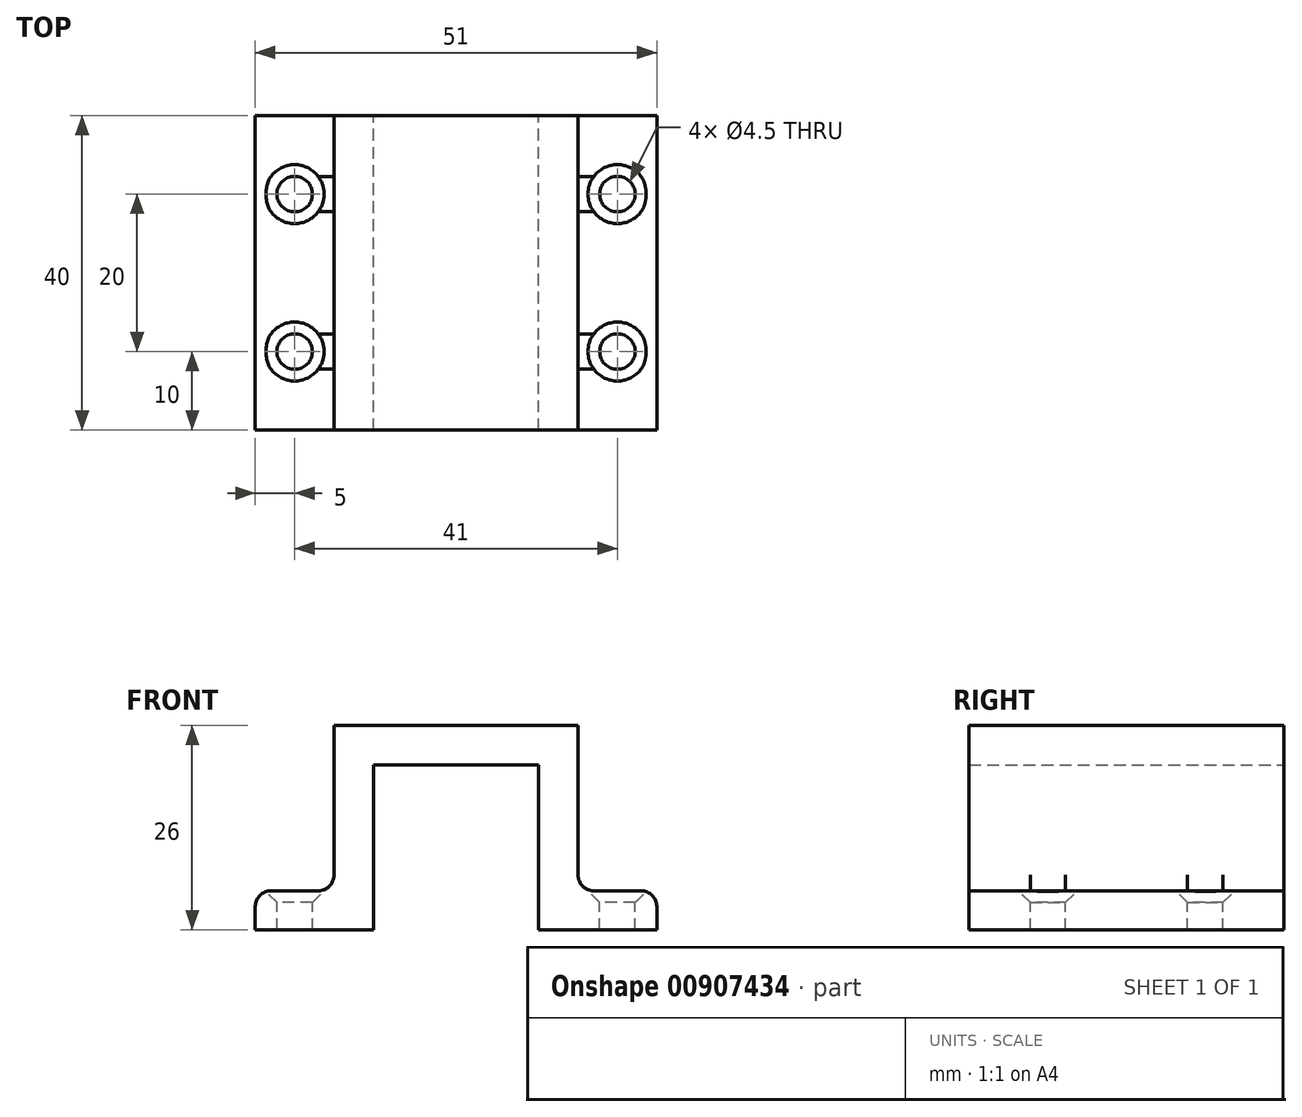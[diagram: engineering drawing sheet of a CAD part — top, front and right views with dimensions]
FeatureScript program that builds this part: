
annotation { "Feature Type Name" : "Feature", "Feature Type Description" : "" }
export const myFeature = defineFeature(function(context is Context, id is Id, definition is map)
    precondition{}
    {
        {
            var Q0;
            Q0=qCreatedBy(makeId("Front.planeOp"),FACE);
            var sketch = newSketch(context, id + "F0", { "sketchPlane" : qUnion([Q0])});
            skLineSegment(sketch, "E0", {"start": v(10.5, 0) * mm, "end": v(21, 0) * mm});
            skLineSegment(sketch, "E1", {"start": v(21, 0) * mm, "end": v(21, -21) * mm});
            skLineSegment(sketch, "E2", {"start": v(21, -21) * mm, "end": v(31, -21) * mm});
            skLineSegment(sketch, "E3", {"start": v(31, -16) * mm, "end": v(26, -16) * mm});
            skLineSegment(sketch, "E4", {"start": v(26, -16) * mm, "end": v(26, 5) * mm});
            skLineSegment(sketch, "E5.0", {"start": v(10.5, 5) * mm, "end": v(21, 5) * mm});
            skLineSegment(sketch, "E6", {"start": v(21, 5) * mm, "end": v(26, 5) * mm});
            skPoint(sketch, "E7.orphan", {"position": v(0, 0) * mm});
            skLineSegment(sketch, "E8.MirrorCS", {"start": v(10.5, 5) * mm, "end": v(0, 5) * mm});
            skLineSegment(sketch, "E9.MirrorCS", {"start": v(0, 5) * mm, "end": v(-5, 5) * mm});
            skLineSegment(sketch, "E10.MirrorCS", {"start": v(10.5, 0) * mm, "end": v(0, 0) * mm});
            skLineSegment(sketch, "E11.MirrorCS", {"start": v(-5, -16) * mm, "end": v(-5, 5) * mm});
            skLineSegment(sketch, "E12.MirrorCS", {"start": v(0, 0) * mm, "end": v(0, -21) * mm});
            skLineSegment(sketch, "E13.MirrorCS", {"start": v(0, -21) * mm, "end": v(-10, -21) * mm});
            skLineSegment(sketch, "E14.MirrorCS", {"start": v(-10, -16) * mm, "end": v(-5, -16) * mm});
            skLineSegment(sketch, "E15", {"start": v(31, -16) * mm, "end": v(36, -16) * mm});
            skLineSegment(sketch, "E16", {"start": v(36, -16) * mm, "end": v(36, -21) * mm});
            skLineSegment(sketch, "E17", {"start": v(36, -21) * mm, "end": v(31, -21) * mm});
            skLineSegment(sketch, "E18.MirrorCS", {"start": v(-10, -16) * mm, "end": v(-15, -16) * mm});
            skLineSegment(sketch, "E19.MirrorCS", {"start": v(-15, -16) * mm, "end": v(-15, -21) * mm});
            skLineSegment(sketch, "E20.MirrorCS", {"start": v(-15, -21) * mm, "end": v(-10, -21) * mm});
            skSolve(sketch);
        }
        {
            var Q0;
            Q0 = qSketchRegion(id + "F0", true);
            extrude(context, id + "F1", {"entities" : qUnion([Q0]), "depth" : 40 * mm, "offsetDistance" : 25 * mm});
        }
        {
            var Q0;
            Q0=makeQuery(id+"F1.opExtrude","SWEPT_FACE",FACE,{"disambiguationData":[OSD([sQuery(id+"F0.wireOp",EDGE,"E5.0"),sQuery(id+"F0.wireOp",EDGE,"E6"),sQuery(id+"F0.wireOp",EDGE,"E8.MirrorCS"),sQuery(id+"F0.wireOp",EDGE,"E9.MirrorCS")])]});
            var sketch = newSketch(context, id + "F2", { "sketchPlane" : qUnion([Q0])});
            skLineSegment(sketch, "E21", {"start": v(26, 0) * mm, "end": v(36, 0) * mm});
            skCircle(sketch, "E22", {"center": v(31, -10) * mm, "radius": 2.25 * mm});
            skCircle(sketch, "E23.MirrorC", {"center": v(31, -30) * mm, "radius": 2.25 * mm});
            skCircle(sketch, "E24.MirrorC", {"center": v(-10, -10) * mm, "radius": 2.25 * mm});
            skCircle(sketch, "E25.MirrorC", {"center": v(-10, -30) * mm, "radius": 2.25 * mm});
            skSolve(sketch);
        }
        {
            var Q0;
            Q0 = qSketchRegion(id + "F2", true);
            extrude(context, id + "F3", {"entities" : qUnion([Q0]), "operationType" : NewBodyOperationType.REMOVE, "endBound" : BoundingType.THROUGH_ALL, "oppositeDirection" : true, "depth" : 25 * mm, "offsetDistance" : 25 * mm});
        }
        {
            var Q0;
            Q0=makeQuery(id+"F3.boolean.opBoolean","INTERSECT",EDGE,{"derivedFrom":[makeQuery(id+"F1.opExtrude","SWEPT_FACE",FACE,{"disambiguationData":[OSD([sQuery(id+"F0.wireOp",EDGE,"E14.MirrorCS"),sQuery(id+"F0.wireOp",EDGE,"E18.MirrorCS")])]}),makeQuery(id+"F3.opExtrude","SWEPT_FACE",FACE,{"disambiguationData":[OSD([sQuery(id+"F2.wireOp",EDGE,"E24.MirrorC")])]})]});
            var Q1;
            Q1=makeQuery(id+"F3.boolean.opBoolean","INTERSECT",EDGE,{"derivedFrom":[makeQuery(id+"F1.opExtrude","SWEPT_FACE",FACE,{"disambiguationData":[OSD([sQuery(id+"F0.wireOp",EDGE,"E14.MirrorCS"),sQuery(id+"F0.wireOp",EDGE,"E18.MirrorCS")])]}),makeQuery(id+"F3.opExtrude","SWEPT_FACE",FACE,{"disambiguationData":[OSD([sQuery(id+"F2.wireOp",EDGE,"E25.MirrorC")])]})]});
            var Q2;
            Q2=makeQuery(id+"F3.boolean.opBoolean","INTERSECT",EDGE,{"derivedFrom":[makeQuery(id+"F1.opExtrude","SWEPT_FACE",FACE,{"disambiguationData":[OSD([sQuery(id+"F0.wireOp",EDGE,"E3"),sQuery(id+"F0.wireOp",EDGE,"E15")])]}),makeQuery(id+"F3.opExtrude","SWEPT_FACE",FACE,{"disambiguationData":[OSD([sQuery(id+"F2.wireOp",EDGE,"E22")])]})]});
            var Q3;
            Q3=makeQuery(id+"F3.boolean.opBoolean","INTERSECT",EDGE,{"derivedFrom":[makeQuery(id+"F1.opExtrude","SWEPT_FACE",FACE,{"disambiguationData":[OSD([sQuery(id+"F0.wireOp",EDGE,"E3"),sQuery(id+"F0.wireOp",EDGE,"E15")])]}),makeQuery(id+"F3.opExtrude","SWEPT_FACE",FACE,{"disambiguationData":[OSD([sQuery(id+"F2.wireOp",EDGE,"E23.MirrorC")])]})]});
            chamfer(context, id + "F4", {"entities" : qUnion([Q0, Q1, Q2, Q3]), "width" : 1.5 * mm, "tangentPropagation" : true});
        }
        {
            var Q0;
            Q0=makeQuery(id+"F1.opExtrude","SWEPT_EDGE",EDGE,{"disambiguationData":[OSD([sQuery(id+"F0.wireOp",EDGE,"E11.MirrorCS"),sQuery(id+"F0.wireOp",EDGE,"E14.MirrorCS")])]});
            var Q1;
            Q1=makeQuery(id+"F1.opExtrude","SWEPT_EDGE",EDGE,{"disambiguationData":[OSD([sQuery(id+"F0.wireOp",EDGE,"E3"),sQuery(id+"F0.wireOp",EDGE,"E4")])]});
            var Q2;
            Q2=makeQuery(id+"F1.opExtrude","SWEPT_EDGE",EDGE,{"disambiguationData":[OSD([sQuery(id+"F0.wireOp",EDGE,"E15"),sQuery(id+"F0.wireOp",EDGE,"E16")])]});
            var Q3;
            Q3=makeQuery(id+"F1.opExtrude","SWEPT_EDGE",EDGE,{"disambiguationData":[OSD([sQuery(id+"F0.wireOp",EDGE,"E18.MirrorCS"),sQuery(id+"F0.wireOp",EDGE,"E19.MirrorCS")])]});
            fillet(context, id + "F5", {"entities" : qUnion([Q0, Q1, Q2, Q3]), "radius" : 2 * mm, "tangentPropagation" : true, "allowEdgeOverflow" : false});
        }
    });
